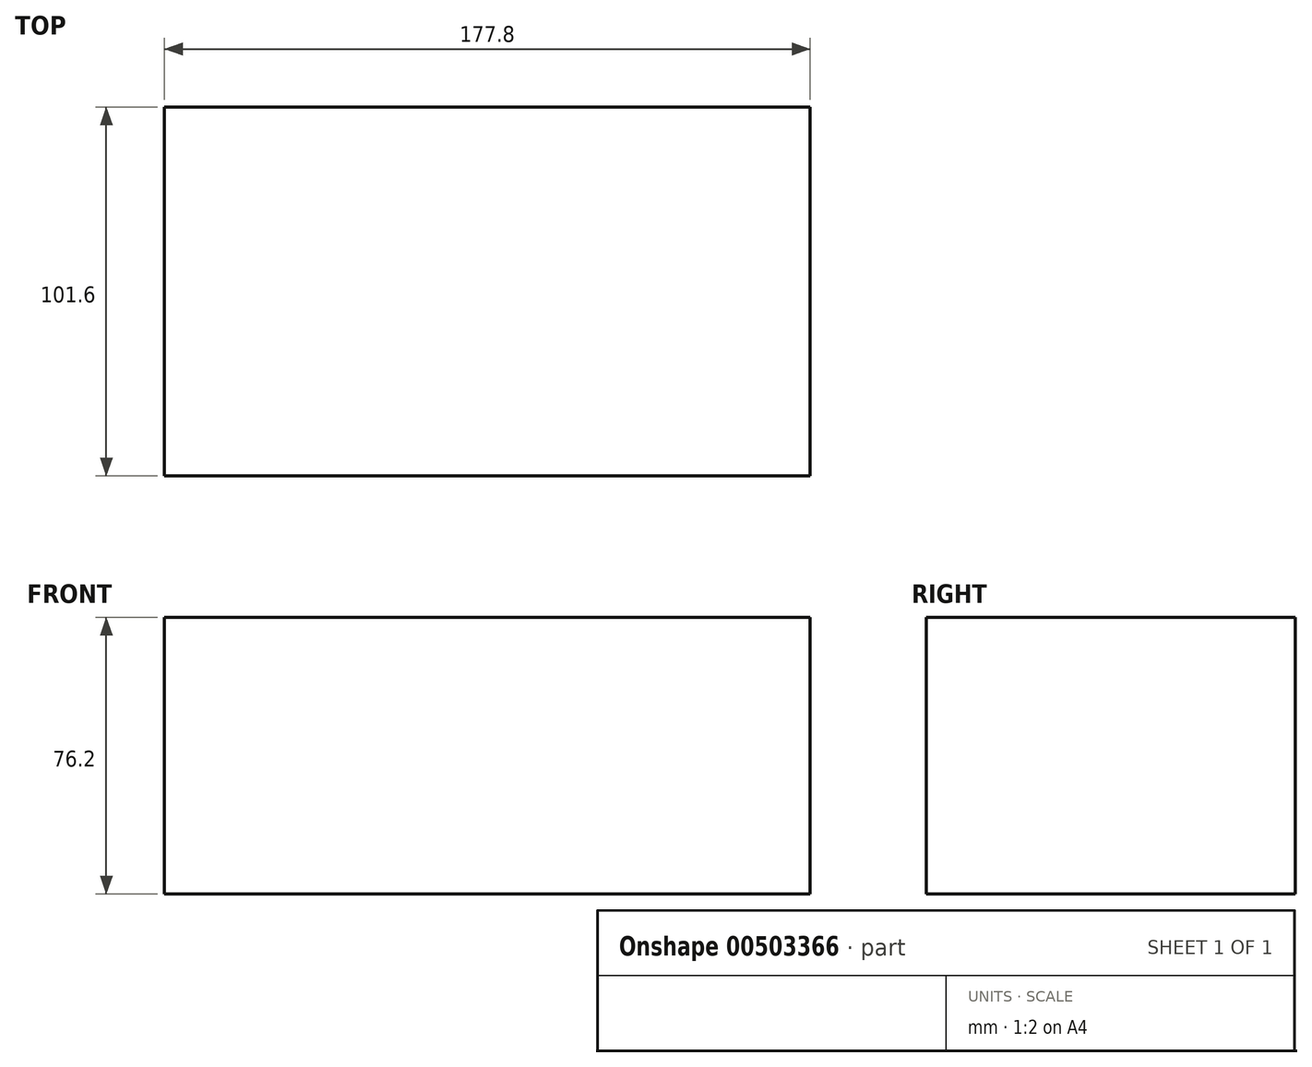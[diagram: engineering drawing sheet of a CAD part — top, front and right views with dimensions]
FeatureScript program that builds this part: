
annotation { "Feature Type Name" : "Feature", "Feature Type Description" : "" }
export const myFeature = defineFeature(function(context is Context, id is Id, definition is map)
    precondition{}
    {
        {
            var Q0;
            Q0=qCreatedBy(makeId("Top.planeOp"),FACE);
            var sketch = newSketch(context, id + "F0", { "sketchPlane" : qUnion([Q0])});
            skLineSegment(sketch, "E0.bottom", {"start": v(88.9, 50.8) * mm, "end": v(-88.9, 50.8) * mm});
            skLineSegment(sketch, "E0.top", {"start": v(88.9, -50.8) * mm, "end": v(-88.9, -50.8) * mm});
            skLineSegment(sketch, "E0.left", {"start": v(88.9, 50.8) * mm, "end": v(88.9, -50.8) * mm});
            skLineSegment(sketch, "E0.right", {"start": v(-88.9, 50.8) * mm, "end": v(-88.9, -50.8) * mm});
            skPoint(sketch, "E0.middle", {"position": v(0, 0) * mm});
            skSolve(sketch);
        }
        {
            var Q0;
            Q0=makeQuery(id+"F0.imprint","IMPRINT",FACE,{"disambiguationData":[TD([[makeQuery(id+"F0.imprint","IMPRINT",EDGE,{"derivedFrom":sQuery(id+"F0.wireOp",EDGE,"E0.bottom")}),1.0]])]});
            extrude(context, id + "F1", {"entities" : qUnion([Q0]), "depth" : 76.2 * mm});
        }
    });
